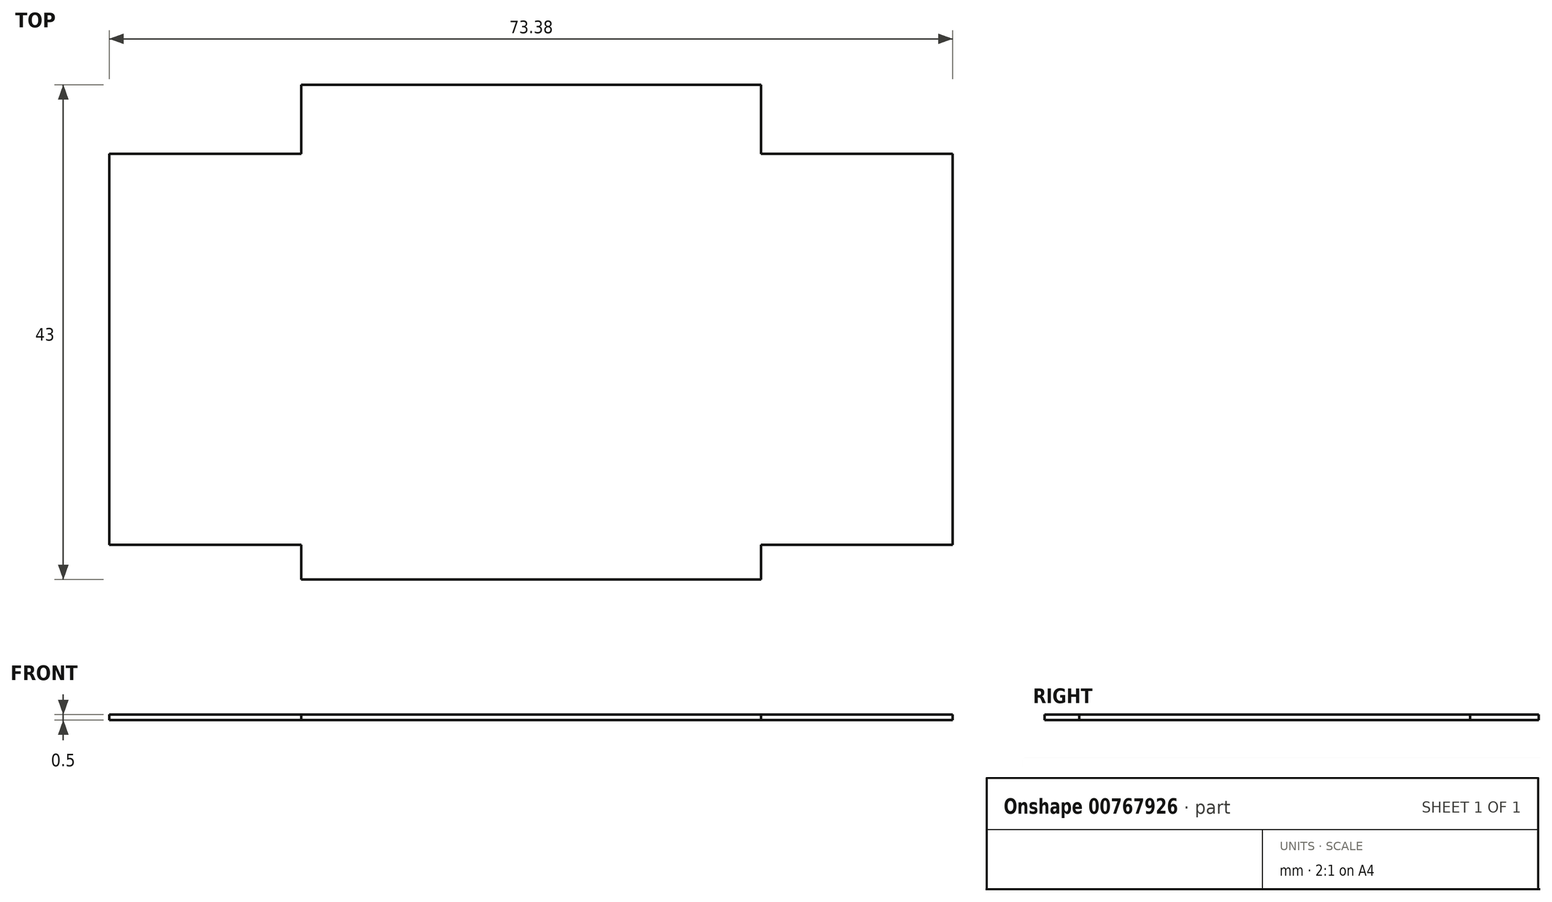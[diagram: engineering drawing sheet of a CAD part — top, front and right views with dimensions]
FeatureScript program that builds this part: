
annotation { "Feature Type Name" : "Feature", "Feature Type Description" : "" }
export const myFeature = defineFeature(function(context is Context, id is Id, definition is map)
    precondition{}
    {
        {
            var Q0;
            Q0=qCreatedBy(makeId("Top.planeOp"),FACE);
            var sketch = newSketch(context, id + "F0", { "sketchPlane" : qUnion([Q0])});
            skLineSegment(sketch, "E0.bottom", {"start": v(0, 0) * mm, "end": v(16.7, 0) * mm});
            skLineSegment(sketch, "E0.top", {"start": v(0, 34) * mm, "end": v(16.69, 34) * mm});
            skLineSegment(sketch, "E0.left", {"start": v(0, 0) * mm, "end": v(0, 34) * mm});
            skLineSegment(sketch, "E0.right", {"start": v(73.38, 0) * mm, "end": v(73.38, 34) * mm});
            skLineSegment(sketch, "E1", {"start": v(16.69, 41.38) * mm, "end": v(16.7, -8.02) * mm, "construction": true});
            skLineSegment(sketch, "E2.0", {"start": v(56.69, 41.38) * mm, "end": v(56.7, -8.02) * mm, "construction": true});
            skLineSegment(sketch, "E3", {"start": v(16.69, 34) * mm, "end": v(16.69, 40) * mm});
            skLineSegment(sketch, "E4", {"start": v(16.69, 40) * mm, "end": v(56.7, 40) * mm});
            skLineSegment(sketch, "E5", {"start": v(56.69, 40) * mm, "end": v(56.69, 34) * mm});
            skLineSegment(sketch, "E6", {"start": v(16.7, 0) * mm, "end": v(16.7, -3) * mm});
            skLineSegment(sketch, "E7", {"start": v(16.7, -3) * mm, "end": v(56.7, -3) * mm});
            skLineSegment(sketch, "E8", {"start": v(56.7, -3) * mm, "end": v(56.7, 0) * mm});
            skLineSegment(sketch, "E9.trimOffspring", {"start": v(56.7, 0) * mm, "end": v(73.38, 0) * mm});
            skLineSegment(sketch, "E10.trimOffspring", {"start": v(56.69, 34) * mm, "end": v(73.38, 34) * mm});
            skSolve(sketch);
        }
        {
            var Q0;
            Q0=makeQuery(id+"F0.imprint","IMPRINT",FACE,{"disambiguationData":[TD([[makeQuery(id+"F0.imprint","IMPRINT",EDGE,{"derivedFrom":sQuery(id+"F0.wireOp",EDGE,"E0.bottom")}),1.0]])]});
            extrude(context, id + "F1", {"entities" : qUnion([Q0]), "depth" : 0.5 * mm, "offsetDistance" : 25 * mm});
        }
    });
